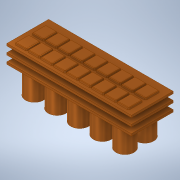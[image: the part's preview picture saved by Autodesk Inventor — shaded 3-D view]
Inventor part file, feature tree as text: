
AUTODESK INVENTOR PART (.ipt)
format: ipt  version: 2020 (Build 240168000, 168)  size: 637,952 bytes
history: native  units: mm
features: chamfer x16, extrude x9, sketch x9, other x2
ambient origin geometry x8: Origin, YZ Plane, XZ Plane, XY Plane, X Axis, Y Axis, Z Axis, Center Point
bodies: Body1 (feature_tree)
feature tree (36):
  other  "Bryła1"
  extrude  "Wyciągnięcie proste1"  Depth=18.73mm
  extrude  "Wyciągnięcie proste2"  Depth=9.365mm
  chamfer  "Faza1"  Distance=55.88mm
  chamfer  "Faza2"  Distance=27.94mm
  chamfer  "Faza3"  Distance=1.0mm
  extrude  "Wyciągnięcie proste3"  Depth=6.03mm
  chamfer  "Faza4"  Distance=5.08mm
  extrude  "Wyciągnięcie proste4"  Depth=2.54mm
  chamfer  "Faza5"  Distance=1.27mm
  chamfer  "Faza6"  Distance=5.08mm
  chamfer  "Faza7"  Distance=6.03mm
  chamfer  "Faza8"  Distance=1.27mm
  chamfer  "Faza9"  Distance=0.64mm
  chamfer  "Faza10"  Distance=5.08mm
  chamfer  "Faza11"  Distance=0.64mm
  chamfer  "Faza12"  Distance=5.08mm
  chamfer  "Faza13"  Distance=0.64mm
  chamfer  "Faza14"  Distance=5.08mm
  chamfer  "Faza15"  Distance=0.64mm
  chamfer  "Faza16"  Distance=5.08mm
  other  "Płaszczyzna konstrukcyjna1"
  extrude  "Wyciągnięcie proste5"  Depth=5.08mm
  extrude  "Wyciągnięcie proste6"  Depth=5.08mm
  extrude  "Wyciągnięcie proste7"  Depth=5.08mm
  extrude  "Wyciągnięcie proste8"  Depth=0.64mm
  extrude  "Wyciągnięcie proste9"  Depth=0.64mm
  sketch  "Szkic1"
  sketch  "Szkic2"
  sketch  "Szkic3"
  sketch  "Szkic4"
  sketch  "Szkic5"
  sketch  "Szkic6"
  sketch  "Szkic7"
  sketch  "Szkic8"
  sketch  "Szkic9"
